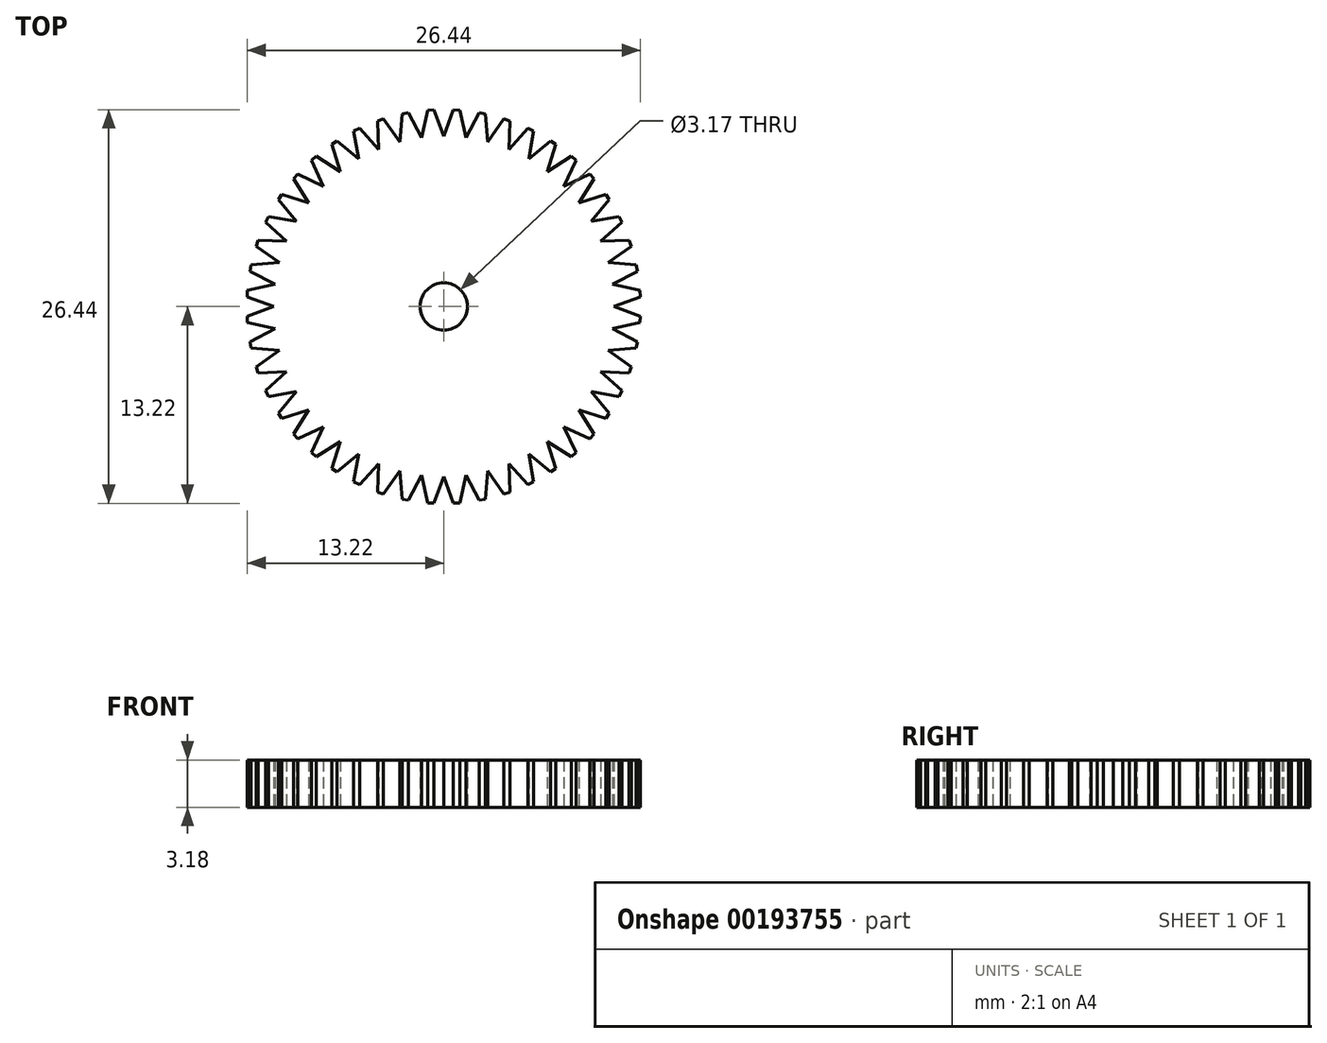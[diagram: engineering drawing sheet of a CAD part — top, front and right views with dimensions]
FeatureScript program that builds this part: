
annotation { "Feature Type Name" : "Feature", "Feature Type Description" : "" }
export const myFeature = defineFeature(function(context is Context, id is Id, definition is map)
    precondition{}
    {
        {
            var Q0;
            Q0=qCreatedBy(makeId("Top.planeOp"),FACE);
            var sketch = newSketch(context, id + "F0", { "sketchPlane" : qUnion([Q0])});
            skCircle(sketch, "E0", {"center": v(0, 0) * mm, "radius": 12.7 * mm});
            skCircle(sketch, "E1", {"center": v(0, 0) * mm, "radius": 13.23 * mm});
            skCircle(sketch, "E2", {"center": v(0, 0) * mm, "radius": 11.43 * mm});
            skLineSegment(sketch, "E3", {"start": v(0, 0) * mm, "end": v(0, 11.43) * mm});
            skLineSegment(sketch, "E4.1.0", {"start": v(0, 0) * mm, "end": v(-1.5, 11.33) * mm});
            skLineSegment(sketch, "E4.2.0", {"start": v(0, 0) * mm, "end": v(-2.96, 11.04) * mm});
            skLineSegment(sketch, "E4.3.0", {"start": v(0, 0) * mm, "end": v(-4.37, 10.56) * mm});
            skLineSegment(sketch, "E4.4.0", {"start": v(0, 0) * mm, "end": v(-5.71, 9.9) * mm});
            skLineSegment(sketch, "E4.5.0", {"start": v(0, 0) * mm, "end": v(-6.96, 9.07) * mm});
            skLineSegment(sketch, "E4.6.0", {"start": v(0, 0) * mm, "end": v(-8.08, 8.08) * mm});
            skLineSegment(sketch, "E4.7.0", {"start": v(0, 0) * mm, "end": v(-9.07, 6.96) * mm});
            skLineSegment(sketch, "E4.8.0", {"start": v(0, 0) * mm, "end": v(-9.9, 5.72) * mm});
            skLineSegment(sketch, "E4.9.0", {"start": v(0, 0) * mm, "end": v(-10.56, 4.37) * mm});
            skLineSegment(sketch, "E4.10.0", {"start": v(0, 0) * mm, "end": v(-11.04, 2.96) * mm});
            skLineSegment(sketch, "E4.11.0", {"start": v(0, 0) * mm, "end": v(-11.33, 1.5) * mm});
            skLineSegment(sketch, "E4.12.0", {"start": v(0, 0) * mm, "end": v(-11.43, 0) * mm});
            skLineSegment(sketch, "E4.13.0", {"start": v(0, 0) * mm, "end": v(-11.33, -1.5) * mm});
            skLineSegment(sketch, "E4.14.0", {"start": v(0, 0) * mm, "end": v(-11.04, -2.96) * mm});
            skLineSegment(sketch, "E4.15.0", {"start": v(0, 0) * mm, "end": v(-10.56, -4.37) * mm});
            skLineSegment(sketch, "E4.16.0", {"start": v(0, 0) * mm, "end": v(-9.9, -5.71) * mm});
            skLineSegment(sketch, "E4.17.0", {"start": v(0, 0) * mm, "end": v(-9.07, -6.96) * mm});
            skLineSegment(sketch, "E4.18.0", {"start": v(0, 0) * mm, "end": v(-8.08, -8.08) * mm});
            skLineSegment(sketch, "E4.19.0", {"start": v(0, 0) * mm, "end": v(-6.96, -9.07) * mm});
            skLineSegment(sketch, "E4.20.0", {"start": v(0, 0) * mm, "end": v(-5.71, -9.9) * mm});
            skLineSegment(sketch, "E4.21.0", {"start": v(0, 0) * mm, "end": v(-4.37, -10.56) * mm});
            skLineSegment(sketch, "E4.22.0", {"start": v(0, 0) * mm, "end": v(-2.96, -11.04) * mm});
            skLineSegment(sketch, "E4.23.0", {"start": v(0, 0) * mm, "end": v(-1.5, -11.33) * mm});
            skLineSegment(sketch, "E4.24.0", {"start": v(0, 0) * mm, "end": v(0, -11.43) * mm});
            skLineSegment(sketch, "E4.25.0", {"start": v(0, 0) * mm, "end": v(1.5, -11.33) * mm});
            skLineSegment(sketch, "E4.26.0", {"start": v(0, 0) * mm, "end": v(2.96, -11.04) * mm});
            skLineSegment(sketch, "E4.27.0", {"start": v(0, 0) * mm, "end": v(4.37, -10.56) * mm});
            skLineSegment(sketch, "E4.28.0", {"start": v(0, 0) * mm, "end": v(5.71, -9.9) * mm});
            skLineSegment(sketch, "E4.29.0", {"start": v(0, 0) * mm, "end": v(6.96, -9.07) * mm});
            skLineSegment(sketch, "E4.30.0", {"start": v(0, 0) * mm, "end": v(8.08, -8.08) * mm});
            skLineSegment(sketch, "E4.31.0", {"start": v(0, 0) * mm, "end": v(9.07, -6.96) * mm});
            skLineSegment(sketch, "E4.32.0", {"start": v(0, 0) * mm, "end": v(9.9, -5.71) * mm});
            skLineSegment(sketch, "E4.33.0", {"start": v(0, 0) * mm, "end": v(10.56, -4.37) * mm});
            skLineSegment(sketch, "E4.34.0", {"start": v(0, 0) * mm, "end": v(11.04, -2.96) * mm});
            skLineSegment(sketch, "E4.35.0", {"start": v(0, 0) * mm, "end": v(11.33, -1.5) * mm});
            skLineSegment(sketch, "E4.36.0", {"start": v(0, 0) * mm, "end": v(11.43, 0) * mm});
            skLineSegment(sketch, "E4.37.0", {"start": v(0, 0) * mm, "end": v(11.33, 1.5) * mm});
            skLineSegment(sketch, "E4.38.0", {"start": v(0, 0) * mm, "end": v(11.04, 2.96) * mm});
            skLineSegment(sketch, "E4.39.0", {"start": v(0, 0) * mm, "end": v(10.56, 4.37) * mm});
            skLineSegment(sketch, "E4.40.0", {"start": v(0, 0) * mm, "end": v(9.9, 5.71) * mm});
            skLineSegment(sketch, "E4.41.0", {"start": v(0, 0) * mm, "end": v(9.07, 6.96) * mm});
            skLineSegment(sketch, "E4.42.0", {"start": v(0, 0) * mm, "end": v(8.08, 8.08) * mm});
            skLineSegment(sketch, "E4.43.0", {"start": v(0, 0) * mm, "end": v(6.96, 9.07) * mm});
            skLineSegment(sketch, "E4.44.0", {"start": v(0, 0) * mm, "end": v(5.72, 9.9) * mm});
            skLineSegment(sketch, "E4.45.0", {"start": v(0, 0) * mm, "end": v(4.37, 10.56) * mm});
            skLineSegment(sketch, "E4.46.0", {"start": v(0, 0) * mm, "end": v(2.96, 11.04) * mm});
            skLineSegment(sketch, "E4.47.0", {"start": v(0, 0) * mm, "end": v(1.5, 11.33) * mm});
            skSolve(sketch);
        }
        {
            var Q0;
            Q0=qCreatedBy(makeId("Top.planeOp"),FACE);
            var sketch = newSketch(context, id + "F1", { "sketchPlane" : qUnion([Q0])});
            skLineSegment(sketch, "E5", {"start": v(0, 11.43) * mm, "end": v(0.65, 13.22) * mm});
            skLineSegment(sketch, "E6", {"start": v(1.08, 13.19) * mm, "end": v(1.5, 11.33) * mm});
            skLineSegment(sketch, "E7", {"start": v(1.08, 13.19) * mm, "end": v(0.65, 13.22) * mm});
            skLineSegment(sketch, "E8.1.0", {"start": v(-1.5, 11.33) * mm, "end": v(-1.08, 13.19) * mm});
            skLineSegment(sketch, "E8.1.1", {"start": v(-0.65, 13.22) * mm, "end": v(-1.08, 13.19) * mm});
            skLineSegment(sketch, "E8.1.2", {"start": v(-0.65, 13.22) * mm, "end": v(0, 11.43) * mm});
            skLineSegment(sketch, "E8.2.0", {"start": v(-2.96, 11.04) * mm, "end": v(-2.8, 12.94) * mm});
            skLineSegment(sketch, "E8.2.1", {"start": v(-2.37, 13.02) * mm, "end": v(-2.8, 12.94) * mm});
            skLineSegment(sketch, "E8.2.2", {"start": v(-2.37, 13.02) * mm, "end": v(-1.5, 11.33) * mm});
            skLineSegment(sketch, "E8.3.0", {"start": v(-4.37, 10.56) * mm, "end": v(-4.46, 12.46) * mm});
            skLineSegment(sketch, "E8.3.1", {"start": v(-4.05, 12.6) * mm, "end": v(-4.46, 12.46) * mm});
            skLineSegment(sketch, "E8.3.2", {"start": v(-4.05, 12.6) * mm, "end": v(-2.96, 11.04) * mm});
            skLineSegment(sketch, "E8.4.0", {"start": v(-5.71, 9.9) * mm, "end": v(-6.05, 11.77) * mm});
            skLineSegment(sketch, "E8.4.1", {"start": v(-5.66, 11.96) * mm, "end": v(-6.05, 11.77) * mm});
            skLineSegment(sketch, "E8.4.2", {"start": v(-5.66, 11.96) * mm, "end": v(-4.37, 10.56) * mm});
            skLineSegment(sketch, "E8.5.0", {"start": v(-6.96, 9.07) * mm, "end": v(-7.53, 10.88) * mm});
            skLineSegment(sketch, "E8.5.1", {"start": v(-7.17, 11.12) * mm, "end": v(-7.53, 10.88) * mm});
            skLineSegment(sketch, "E8.5.2", {"start": v(-7.17, 11.12) * mm, "end": v(-5.72, 9.9) * mm});
            skLineSegment(sketch, "E8.6.0", {"start": v(-8.08, 8.08) * mm, "end": v(-8.89, 9.8) * mm});
            skLineSegment(sketch, "E8.6.1", {"start": v(-8.56, 10.1) * mm, "end": v(-8.89, 9.8) * mm});
            skLineSegment(sketch, "E8.6.2", {"start": v(-8.56, 10.1) * mm, "end": v(-6.96, 9.07) * mm});
            skLineSegment(sketch, "E8.7.0", {"start": v(-9.07, 6.96) * mm, "end": v(-10.1, 8.56) * mm});
            skLineSegment(sketch, "E8.7.1", {"start": v(-9.8, 8.89) * mm, "end": v(-10.1, 8.56) * mm});
            skLineSegment(sketch, "E8.7.2", {"start": v(-9.8, 8.89) * mm, "end": v(-8.08, 8.08) * mm});
            skLineSegment(sketch, "E8.8.0", {"start": v(-9.9, 5.72) * mm, "end": v(-11.12, 7.17) * mm});
            skLineSegment(sketch, "E8.8.1", {"start": v(-10.88, 7.53) * mm, "end": v(-11.12, 7.17) * mm});
            skLineSegment(sketch, "E8.8.2", {"start": v(-10.88, 7.53) * mm, "end": v(-9.07, 6.96) * mm});
            skLineSegment(sketch, "E8.9.0", {"start": v(-10.56, 4.37) * mm, "end": v(-11.96, 5.66) * mm});
            skLineSegment(sketch, "E8.9.1", {"start": v(-11.77, 6.05) * mm, "end": v(-11.96, 5.66) * mm});
            skLineSegment(sketch, "E8.9.2", {"start": v(-11.77, 6.05) * mm, "end": v(-9.9, 5.71) * mm});
            skLineSegment(sketch, "E8.10.0", {"start": v(-11.04, 2.96) * mm, "end": v(-12.6, 4.05) * mm});
            skLineSegment(sketch, "E8.10.1", {"start": v(-12.46, 4.46) * mm, "end": v(-12.6, 4.05) * mm});
            skLineSegment(sketch, "E8.10.2", {"start": v(-12.46, 4.46) * mm, "end": v(-10.56, 4.37) * mm});
            skLineSegment(sketch, "E8.11.0", {"start": v(-11.33, 1.5) * mm, "end": v(-13.02, 2.37) * mm});
            skLineSegment(sketch, "E8.11.1", {"start": v(-12.94, 2.8) * mm, "end": v(-13.02, 2.37) * mm});
            skLineSegment(sketch, "E8.11.2", {"start": v(-12.94, 2.8) * mm, "end": v(-11.04, 2.96) * mm});
            skLineSegment(sketch, "E8.12.0", {"start": v(-11.43, 0) * mm, "end": v(-13.22, 0.65) * mm});
            skLineSegment(sketch, "E8.12.1", {"start": v(-13.19, 1.08) * mm, "end": v(-13.22, 0.65) * mm});
            skLineSegment(sketch, "E8.12.2", {"start": v(-13.19, 1.08) * mm, "end": v(-11.33, 1.5) * mm});
            skLineSegment(sketch, "E8.13.0", {"start": v(-11.33, -1.5) * mm, "end": v(-13.19, -1.08) * mm});
            skLineSegment(sketch, "E8.13.1", {"start": v(-13.22, -0.65) * mm, "end": v(-13.19, -1.08) * mm});
            skLineSegment(sketch, "E8.13.2", {"start": v(-13.22, -0.65) * mm, "end": v(-11.43, 0) * mm});
            skLineSegment(sketch, "E8.14.0", {"start": v(-11.04, -2.96) * mm, "end": v(-12.94, -2.8) * mm});
            skLineSegment(sketch, "E8.14.1", {"start": v(-13.02, -2.37) * mm, "end": v(-12.94, -2.8) * mm});
            skLineSegment(sketch, "E8.14.2", {"start": v(-13.02, -2.37) * mm, "end": v(-11.33, -1.5) * mm});
            skLineSegment(sketch, "E8.15.0", {"start": v(-10.56, -4.37) * mm, "end": v(-12.46, -4.46) * mm});
            skLineSegment(sketch, "E8.15.1", {"start": v(-12.6, -4.05) * mm, "end": v(-12.46, -4.46) * mm});
            skLineSegment(sketch, "E8.15.2", {"start": v(-12.6, -4.05) * mm, "end": v(-11.04, -2.96) * mm});
            skLineSegment(sketch, "E8.16.0", {"start": v(-9.9, -5.71) * mm, "end": v(-11.77, -6.05) * mm});
            skLineSegment(sketch, "E8.16.1", {"start": v(-11.96, -5.66) * mm, "end": v(-11.77, -6.05) * mm});
            skLineSegment(sketch, "E8.16.2", {"start": v(-11.96, -5.66) * mm, "end": v(-10.56, -4.37) * mm});
            skLineSegment(sketch, "E8.17.0", {"start": v(-9.07, -6.96) * mm, "end": v(-10.88, -7.53) * mm});
            skLineSegment(sketch, "E8.17.1", {"start": v(-11.12, -7.17) * mm, "end": v(-10.88, -7.53) * mm});
            skLineSegment(sketch, "E8.17.2", {"start": v(-11.12, -7.17) * mm, "end": v(-9.9, -5.72) * mm});
            skLineSegment(sketch, "E8.18.0", {"start": v(-8.08, -8.08) * mm, "end": v(-9.8, -8.89) * mm});
            skLineSegment(sketch, "E8.18.1", {"start": v(-10.1, -8.56) * mm, "end": v(-9.8, -8.89) * mm});
            skLineSegment(sketch, "E8.18.2", {"start": v(-10.1, -8.56) * mm, "end": v(-9.07, -6.96) * mm});
            skLineSegment(sketch, "E8.19.0", {"start": v(-6.96, -9.07) * mm, "end": v(-8.56, -10.1) * mm});
            skLineSegment(sketch, "E8.19.1", {"start": v(-8.89, -9.8) * mm, "end": v(-8.56, -10.1) * mm});
            skLineSegment(sketch, "E8.19.2", {"start": v(-8.89, -9.8) * mm, "end": v(-8.08, -8.08) * mm});
            skLineSegment(sketch, "E8.20.0", {"start": v(-5.71, -9.9) * mm, "end": v(-7.17, -11.12) * mm});
            skLineSegment(sketch, "E8.20.1", {"start": v(-7.53, -10.88) * mm, "end": v(-7.17, -11.12) * mm});
            skLineSegment(sketch, "E8.20.2", {"start": v(-7.53, -10.88) * mm, "end": v(-6.96, -9.07) * mm});
            skLineSegment(sketch, "E8.21.0", {"start": v(-4.37, -10.56) * mm, "end": v(-5.66, -11.96) * mm});
            skLineSegment(sketch, "E8.21.1", {"start": v(-6.05, -11.77) * mm, "end": v(-5.66, -11.96) * mm});
            skLineSegment(sketch, "E8.21.2", {"start": v(-6.05, -11.77) * mm, "end": v(-5.72, -9.9) * mm});
            skLineSegment(sketch, "E8.22.0", {"start": v(-2.96, -11.04) * mm, "end": v(-4.05, -12.6) * mm});
            skLineSegment(sketch, "E8.22.1", {"start": v(-4.46, -12.46) * mm, "end": v(-4.05, -12.6) * mm});
            skLineSegment(sketch, "E8.22.2", {"start": v(-4.46, -12.46) * mm, "end": v(-4.37, -10.56) * mm});
            skLineSegment(sketch, "E8.23.0", {"start": v(-1.5, -11.33) * mm, "end": v(-2.37, -13.02) * mm});
            skLineSegment(sketch, "E8.23.1", {"start": v(-2.8, -12.94) * mm, "end": v(-2.37, -13.02) * mm});
            skLineSegment(sketch, "E8.23.2", {"start": v(-2.8, -12.94) * mm, "end": v(-2.96, -11.04) * mm});
            skLineSegment(sketch, "E8.24.0", {"start": v(0, -11.43) * mm, "end": v(-0.65, -13.22) * mm});
            skLineSegment(sketch, "E8.24.1", {"start": v(-1.08, -13.19) * mm, "end": v(-0.65, -13.22) * mm});
            skLineSegment(sketch, "E8.24.2", {"start": v(-1.08, -13.19) * mm, "end": v(-1.5, -11.33) * mm});
            skLineSegment(sketch, "E8.25.0", {"start": v(1.5, -11.33) * mm, "end": v(1.08, -13.19) * mm});
            skLineSegment(sketch, "E8.25.1", {"start": v(0.65, -13.22) * mm, "end": v(1.08, -13.19) * mm});
            skLineSegment(sketch, "E8.25.2", {"start": v(0.65, -13.22) * mm, "end": v(0, -11.43) * mm});
            skLineSegment(sketch, "E8.26.0", {"start": v(2.96, -11.04) * mm, "end": v(2.8, -12.94) * mm});
            skLineSegment(sketch, "E8.26.1", {"start": v(2.37, -13.02) * mm, "end": v(2.8, -12.94) * mm});
            skLineSegment(sketch, "E8.26.2", {"start": v(2.37, -13.02) * mm, "end": v(1.5, -11.33) * mm});
            skLineSegment(sketch, "E8.27.0", {"start": v(4.37, -10.56) * mm, "end": v(4.46, -12.46) * mm});
            skLineSegment(sketch, "E8.27.1", {"start": v(4.05, -12.6) * mm, "end": v(4.46, -12.46) * mm});
            skLineSegment(sketch, "E8.27.2", {"start": v(4.05, -12.6) * mm, "end": v(2.96, -11.04) * mm});
            skLineSegment(sketch, "E8.28.0", {"start": v(5.71, -9.9) * mm, "end": v(6.05, -11.77) * mm});
            skLineSegment(sketch, "E8.28.1", {"start": v(5.66, -11.96) * mm, "end": v(6.05, -11.77) * mm});
            skLineSegment(sketch, "E8.28.2", {"start": v(5.66, -11.96) * mm, "end": v(4.37, -10.56) * mm});
            skLineSegment(sketch, "E8.29.0", {"start": v(6.96, -9.07) * mm, "end": v(7.53, -10.88) * mm});
            skLineSegment(sketch, "E8.29.1", {"start": v(7.17, -11.12) * mm, "end": v(7.53, -10.88) * mm});
            skLineSegment(sketch, "E8.29.2", {"start": v(7.17, -11.12) * mm, "end": v(5.72, -9.9) * mm});
            skLineSegment(sketch, "E8.30.0", {"start": v(8.08, -8.08) * mm, "end": v(8.89, -9.8) * mm});
            skLineSegment(sketch, "E8.30.1", {"start": v(8.56, -10.1) * mm, "end": v(8.89, -9.8) * mm});
            skLineSegment(sketch, "E8.30.2", {"start": v(8.56, -10.1) * mm, "end": v(6.96, -9.07) * mm});
            skLineSegment(sketch, "E8.31.0", {"start": v(9.07, -6.96) * mm, "end": v(10.1, -8.56) * mm});
            skLineSegment(sketch, "E8.31.1", {"start": v(9.8, -8.89) * mm, "end": v(10.1, -8.56) * mm});
            skLineSegment(sketch, "E8.31.2", {"start": v(9.8, -8.89) * mm, "end": v(8.08, -8.08) * mm});
            skLineSegment(sketch, "E8.32.0", {"start": v(9.9, -5.72) * mm, "end": v(11.12, -7.17) * mm});
            skLineSegment(sketch, "E8.32.1", {"start": v(10.88, -7.53) * mm, "end": v(11.12, -7.17) * mm});
            skLineSegment(sketch, "E8.32.2", {"start": v(10.88, -7.53) * mm, "end": v(9.07, -6.96) * mm});
            skLineSegment(sketch, "E8.33.0", {"start": v(10.56, -4.37) * mm, "end": v(11.96, -5.66) * mm});
            skLineSegment(sketch, "E8.33.1", {"start": v(11.77, -6.05) * mm, "end": v(11.96, -5.66) * mm});
            skLineSegment(sketch, "E8.33.2", {"start": v(11.77, -6.05) * mm, "end": v(9.9, -5.71) * mm});
            skLineSegment(sketch, "E8.34.0", {"start": v(11.04, -2.96) * mm, "end": v(12.6, -4.05) * mm});
            skLineSegment(sketch, "E8.34.1", {"start": v(12.46, -4.46) * mm, "end": v(12.6, -4.05) * mm});
            skLineSegment(sketch, "E8.34.2", {"start": v(12.46, -4.46) * mm, "end": v(10.56, -4.37) * mm});
            skLineSegment(sketch, "E8.35.0", {"start": v(11.33, -1.5) * mm, "end": v(13.02, -2.37) * mm});
            skLineSegment(sketch, "E8.35.1", {"start": v(12.94, -2.8) * mm, "end": v(13.02, -2.37) * mm});
            skLineSegment(sketch, "E8.35.2", {"start": v(12.94, -2.8) * mm, "end": v(11.04, -2.96) * mm});
            skLineSegment(sketch, "E8.36.0", {"start": v(11.43, 0) * mm, "end": v(13.22, -0.65) * mm});
            skLineSegment(sketch, "E8.36.1", {"start": v(13.19, -1.08) * mm, "end": v(13.22, -0.65) * mm});
            skLineSegment(sketch, "E8.36.2", {"start": v(13.19, -1.08) * mm, "end": v(11.33, -1.5) * mm});
            skLineSegment(sketch, "E8.37.0", {"start": v(11.33, 1.5) * mm, "end": v(13.19, 1.08) * mm});
            skLineSegment(sketch, "E8.37.1", {"start": v(13.22, 0.65) * mm, "end": v(13.19, 1.08) * mm});
            skLineSegment(sketch, "E8.37.2", {"start": v(13.22, 0.65) * mm, "end": v(11.43, 0) * mm});
            skLineSegment(sketch, "E8.38.0", {"start": v(11.04, 2.96) * mm, "end": v(12.94, 2.8) * mm});
            skLineSegment(sketch, "E8.38.1", {"start": v(13.02, 2.37) * mm, "end": v(12.94, 2.8) * mm});
            skLineSegment(sketch, "E8.38.2", {"start": v(13.02, 2.37) * mm, "end": v(11.33, 1.5) * mm});
            skLineSegment(sketch, "E8.39.0", {"start": v(10.56, 4.37) * mm, "end": v(12.46, 4.46) * mm});
            skLineSegment(sketch, "E8.39.1", {"start": v(12.6, 4.05) * mm, "end": v(12.46, 4.46) * mm});
            skLineSegment(sketch, "E8.39.2", {"start": v(12.6, 4.05) * mm, "end": v(11.04, 2.96) * mm});
            skLineSegment(sketch, "E8.40.0", {"start": v(9.9, 5.72) * mm, "end": v(11.77, 6.05) * mm});
            skLineSegment(sketch, "E8.40.1", {"start": v(11.96, 5.66) * mm, "end": v(11.77, 6.05) * mm});
            skLineSegment(sketch, "E8.40.2", {"start": v(11.96, 5.66) * mm, "end": v(10.56, 4.37) * mm});
            skLineSegment(sketch, "E8.41.0", {"start": v(9.07, 6.96) * mm, "end": v(10.88, 7.53) * mm});
            skLineSegment(sketch, "E8.41.1", {"start": v(11.12, 7.17) * mm, "end": v(10.88, 7.53) * mm});
            skLineSegment(sketch, "E8.41.2", {"start": v(11.12, 7.17) * mm, "end": v(9.9, 5.71) * mm});
            skLineSegment(sketch, "E8.42.0", {"start": v(8.08, 8.08) * mm, "end": v(9.8, 8.89) * mm});
            skLineSegment(sketch, "E8.42.1", {"start": v(10.1, 8.56) * mm, "end": v(9.8, 8.89) * mm});
            skLineSegment(sketch, "E8.42.2", {"start": v(10.1, 8.56) * mm, "end": v(9.07, 6.96) * mm});
            skLineSegment(sketch, "E8.43.0", {"start": v(6.96, 9.07) * mm, "end": v(8.56, 10.1) * mm});
            skLineSegment(sketch, "E8.43.1", {"start": v(8.89, 9.8) * mm, "end": v(8.56, 10.1) * mm});
            skLineSegment(sketch, "E8.43.2", {"start": v(8.89, 9.8) * mm, "end": v(8.08, 8.08) * mm});
            skLineSegment(sketch, "E8.44.0", {"start": v(5.72, 9.9) * mm, "end": v(7.17, 11.12) * mm});
            skLineSegment(sketch, "E8.44.1", {"start": v(7.53, 10.88) * mm, "end": v(7.17, 11.12) * mm});
            skLineSegment(sketch, "E8.44.2", {"start": v(7.53, 10.88) * mm, "end": v(6.96, 9.07) * mm});
            skLineSegment(sketch, "E8.45.0", {"start": v(4.37, 10.56) * mm, "end": v(5.66, 11.96) * mm});
            skLineSegment(sketch, "E8.45.1", {"start": v(6.05, 11.77) * mm, "end": v(5.66, 11.96) * mm});
            skLineSegment(sketch, "E8.45.2", {"start": v(6.05, 11.77) * mm, "end": v(5.71, 9.9) * mm});
            skLineSegment(sketch, "E8.46.0", {"start": v(2.96, 11.04) * mm, "end": v(4.05, 12.6) * mm});
            skLineSegment(sketch, "E8.46.1", {"start": v(4.46, 12.46) * mm, "end": v(4.05, 12.6) * mm});
            skLineSegment(sketch, "E8.46.2", {"start": v(4.46, 12.46) * mm, "end": v(4.37, 10.56) * mm});
            skLineSegment(sketch, "E8.47.0", {"start": v(1.5, 11.33) * mm, "end": v(2.37, 13.02) * mm});
            skLineSegment(sketch, "E8.47.1", {"start": v(2.8, 12.94) * mm, "end": v(2.37, 13.02) * mm});
            skLineSegment(sketch, "E8.47.2", {"start": v(2.8, 12.94) * mm, "end": v(2.96, 11.04) * mm});
            skPoint(sketch, "E8.center", {"position": v(0, 0) * mm});
            skSolve(sketch);
        }
        {
            var Q0;
            Q0 = qSketchRegion(id + "F1", true);
            extrude(context, id + "F2", {"entities" : qUnion([Q0]), "depth" : 3.17 * mm});
        }
        {
            var Q0;
            Q0=sQuery(id+"F0.wireOp",VERTEX,"E0.center");
            var Q1;
            Q1=makeQuery(id+"F2.opExtrude","SWEPT_BODY",BODY,{"disambiguationData":[OSD([sQuery(id+"F1.wireOp",EDGE,"E5"),sQuery(id+"F1.wireOp",EDGE,"E6"),sQuery(id+"F1.wireOp",EDGE,"E7"),sQuery(id+"F1.wireOp",EDGE,"E8.1.0"),sQuery(id+"F1.wireOp",EDGE,"E8.1.1"),sQuery(id+"F1.wireOp",EDGE,"E8.1.2"),sQuery(id+"F1.wireOp",EDGE,"E8.2.0"),sQuery(id+"F1.wireOp",EDGE,"E8.2.1"),sQuery(id+"F1.wireOp",EDGE,"E8.2.2"),sQuery(id+"F1.wireOp",EDGE,"E8.3.0"),sQuery(id+"F1.wireOp",EDGE,"E8.3.1"),sQuery(id+"F1.wireOp",EDGE,"E8.3.2"),sQuery(id+"F1.wireOp",EDGE,"E8.4.0"),sQuery(id+"F1.wireOp",EDGE,"E8.4.1"),sQuery(id+"F1.wireOp",EDGE,"E8.4.2"),sQuery(id+"F1.wireOp",EDGE,"E8.5.0"),sQuery(id+"F1.wireOp",EDGE,"E8.5.1"),sQuery(id+"F1.wireOp",EDGE,"E8.5.2"),sQuery(id+"F1.wireOp",EDGE,"E8.6.0"),sQuery(id+"F1.wireOp",EDGE,"E8.6.1"),sQuery(id+"F1.wireOp",EDGE,"E8.6.2"),sQuery(id+"F1.wireOp",EDGE,"E8.7.0"),sQuery(id+"F1.wireOp",EDGE,"E8.7.1"),sQuery(id+"F1.wireOp",EDGE,"E8.7.2"),sQuery(id+"F1.wireOp",EDGE,"E8.8.0"),sQuery(id+"F1.wireOp",EDGE,"E8.8.1"),sQuery(id+"F1.wireOp",EDGE,"E8.8.2"),sQuery(id+"F1.wireOp",EDGE,"E8.9.0"),sQuery(id+"F1.wireOp",EDGE,"E8.9.1"),sQuery(id+"F1.wireOp",EDGE,"E8.9.2"),sQuery(id+"F1.wireOp",EDGE,"E8.10.0"),sQuery(id+"F1.wireOp",EDGE,"E8.10.1"),sQuery(id+"F1.wireOp",EDGE,"E8.10.2"),sQuery(id+"F1.wireOp",EDGE,"E8.11.0"),sQuery(id+"F1.wireOp",EDGE,"E8.11.1"),sQuery(id+"F1.wireOp",EDGE,"E8.11.2"),sQuery(id+"F1.wireOp",EDGE,"E8.12.0"),sQuery(id+"F1.wireOp",EDGE,"E8.12.1"),sQuery(id+"F1.wireOp",EDGE,"E8.12.2"),sQuery(id+"F1.wireOp",EDGE,"E8.13.0"),sQuery(id+"F1.wireOp",EDGE,"E8.13.1"),sQuery(id+"F1.wireOp",EDGE,"E8.13.2"),sQuery(id+"F1.wireOp",EDGE,"E8.14.0"),sQuery(id+"F1.wireOp",EDGE,"E8.14.1"),sQuery(id+"F1.wireOp",EDGE,"E8.14.2"),sQuery(id+"F1.wireOp",EDGE,"E8.15.0"),sQuery(id+"F1.wireOp",EDGE,"E8.15.1"),sQuery(id+"F1.wireOp",EDGE,"E8.15.2"),sQuery(id+"F1.wireOp",EDGE,"E8.16.0"),sQuery(id+"F1.wireOp",EDGE,"E8.16.1"),sQuery(id+"F1.wireOp",EDGE,"E8.16.2"),sQuery(id+"F1.wireOp",EDGE,"E8.17.0"),sQuery(id+"F1.wireOp",EDGE,"E8.17.1"),sQuery(id+"F1.wireOp",EDGE,"E8.17.2"),sQuery(id+"F1.wireOp",EDGE,"E8.18.0"),sQuery(id+"F1.wireOp",EDGE,"E8.18.1"),sQuery(id+"F1.wireOp",EDGE,"E8.18.2"),sQuery(id+"F1.wireOp",EDGE,"E8.19.0"),sQuery(id+"F1.wireOp",EDGE,"E8.19.1"),sQuery(id+"F1.wireOp",EDGE,"E8.19.2"),sQuery(id+"F1.wireOp",EDGE,"E8.20.0"),sQuery(id+"F1.wireOp",EDGE,"E8.20.1"),sQuery(id+"F1.wireOp",EDGE,"E8.20.2"),sQuery(id+"F1.wireOp",EDGE,"E8.21.0"),sQuery(id+"F1.wireOp",EDGE,"E8.21.1"),sQuery(id+"F1.wireOp",EDGE,"E8.21.2"),sQuery(id+"F1.wireOp",EDGE,"E8.22.0"),sQuery(id+"F1.wireOp",EDGE,"E8.22.1"),sQuery(id+"F1.wireOp",EDGE,"E8.22.2"),sQuery(id+"F1.wireOp",EDGE,"E8.23.0"),sQuery(id+"F1.wireOp",EDGE,"E8.23.1"),sQuery(id+"F1.wireOp",EDGE,"E8.23.2"),sQuery(id+"F1.wireOp",EDGE,"E8.24.0"),sQuery(id+"F1.wireOp",EDGE,"E8.24.1"),sQuery(id+"F1.wireOp",EDGE,"E8.24.2"),sQuery(id+"F1.wireOp",EDGE,"E8.25.0"),sQuery(id+"F1.wireOp",EDGE,"E8.25.1"),sQuery(id+"F1.wireOp",EDGE,"E8.25.2"),sQuery(id+"F1.wireOp",EDGE,"E8.26.0"),sQuery(id+"F1.wireOp",EDGE,"E8.26.1"),sQuery(id+"F1.wireOp",EDGE,"E8.26.2"),sQuery(id+"F1.wireOp",EDGE,"E8.27.0"),sQuery(id+"F1.wireOp",EDGE,"E8.27.1"),sQuery(id+"F1.wireOp",EDGE,"E8.27.2"),sQuery(id+"F1.wireOp",EDGE,"E8.28.0"),sQuery(id+"F1.wireOp",EDGE,"E8.28.1"),sQuery(id+"F1.wireOp",EDGE,"E8.28.2"),sQuery(id+"F1.wireOp",EDGE,"E8.29.0"),sQuery(id+"F1.wireOp",EDGE,"E8.29.1"),sQuery(id+"F1.wireOp",EDGE,"E8.29.2"),sQuery(id+"F1.wireOp",EDGE,"E8.30.0"),sQuery(id+"F1.wireOp",EDGE,"E8.30.1"),sQuery(id+"F1.wireOp",EDGE,"E8.30.2"),sQuery(id+"F1.wireOp",EDGE,"E8.31.0"),sQuery(id+"F1.wireOp",EDGE,"E8.31.1"),sQuery(id+"F1.wireOp",EDGE,"E8.31.2"),sQuery(id+"F1.wireOp",EDGE,"E8.32.0"),sQuery(id+"F1.wireOp",EDGE,"E8.32.1"),sQuery(id+"F1.wireOp",EDGE,"E8.32.2"),sQuery(id+"F1.wireOp",EDGE,"E8.33.0"),sQuery(id+"F1.wireOp",EDGE,"E8.33.1"),sQuery(id+"F1.wireOp",EDGE,"E8.33.2"),sQuery(id+"F1.wireOp",EDGE,"E8.34.0"),sQuery(id+"F1.wireOp",EDGE,"E8.34.1"),sQuery(id+"F1.wireOp",EDGE,"E8.34.2"),sQuery(id+"F1.wireOp",EDGE,"E8.35.0"),sQuery(id+"F1.wireOp",EDGE,"E8.35.1"),sQuery(id+"F1.wireOp",EDGE,"E8.35.2"),sQuery(id+"F1.wireOp",EDGE,"E8.36.0"),sQuery(id+"F1.wireOp",EDGE,"E8.36.1"),sQuery(id+"F1.wireOp",EDGE,"E8.36.2"),sQuery(id+"F1.wireOp",EDGE,"E8.37.0"),sQuery(id+"F1.wireOp",EDGE,"E8.37.1"),sQuery(id+"F1.wireOp",EDGE,"E8.37.2"),sQuery(id+"F1.wireOp",EDGE,"E8.38.0"),sQuery(id+"F1.wireOp",EDGE,"E8.38.1"),sQuery(id+"F1.wireOp",EDGE,"E8.38.2"),sQuery(id+"F1.wireOp",EDGE,"E8.39.0"),sQuery(id+"F1.wireOp",EDGE,"E8.39.1"),sQuery(id+"F1.wireOp",EDGE,"E8.39.2"),sQuery(id+"F1.wireOp",EDGE,"E8.40.0"),sQuery(id+"F1.wireOp",EDGE,"E8.40.1"),sQuery(id+"F1.wireOp",EDGE,"E8.40.2"),sQuery(id+"F1.wireOp",EDGE,"E8.41.0"),sQuery(id+"F1.wireOp",EDGE,"E8.41.1"),sQuery(id+"F1.wireOp",EDGE,"E8.41.2"),sQuery(id+"F1.wireOp",EDGE,"E8.42.0"),sQuery(id+"F1.wireOp",EDGE,"E8.42.1"),sQuery(id+"F1.wireOp",EDGE,"E8.42.2"),sQuery(id+"F1.wireOp",EDGE,"E8.43.0"),sQuery(id+"F1.wireOp",EDGE,"E8.43.1"),sQuery(id+"F1.wireOp",EDGE,"E8.43.2"),sQuery(id+"F1.wireOp",EDGE,"E8.44.0"),sQuery(id+"F1.wireOp",EDGE,"E8.44.1"),sQuery(id+"F1.wireOp",EDGE,"E8.44.2"),sQuery(id+"F1.wireOp",EDGE,"E8.45.0"),sQuery(id+"F1.wireOp",EDGE,"E8.45.1"),sQuery(id+"F1.wireOp",EDGE,"E8.45.2"),sQuery(id+"F1.wireOp",EDGE,"E8.46.0"),sQuery(id+"F1.wireOp",EDGE,"E8.46.1"),sQuery(id+"F1.wireOp",EDGE,"E8.46.2"),sQuery(id+"F1.wireOp",EDGE,"E8.47.0"),sQuery(id+"F1.wireOp",EDGE,"E8.47.1"),sQuery(id+"F1.wireOp",EDGE,"E8.47.2")])]});
            hole(context, id + "F3", {"style" : HoleStyle.SIMPLE, "endStyle" : HoleEndStyle.THROUGH, "oppositeDirection" : true, "holeDiameter" : 3.17 * mm, "locations" : qUnion([Q0]), "scope" : qUnion([Q1]), "isTappedThrough" : true});
        }
    });
